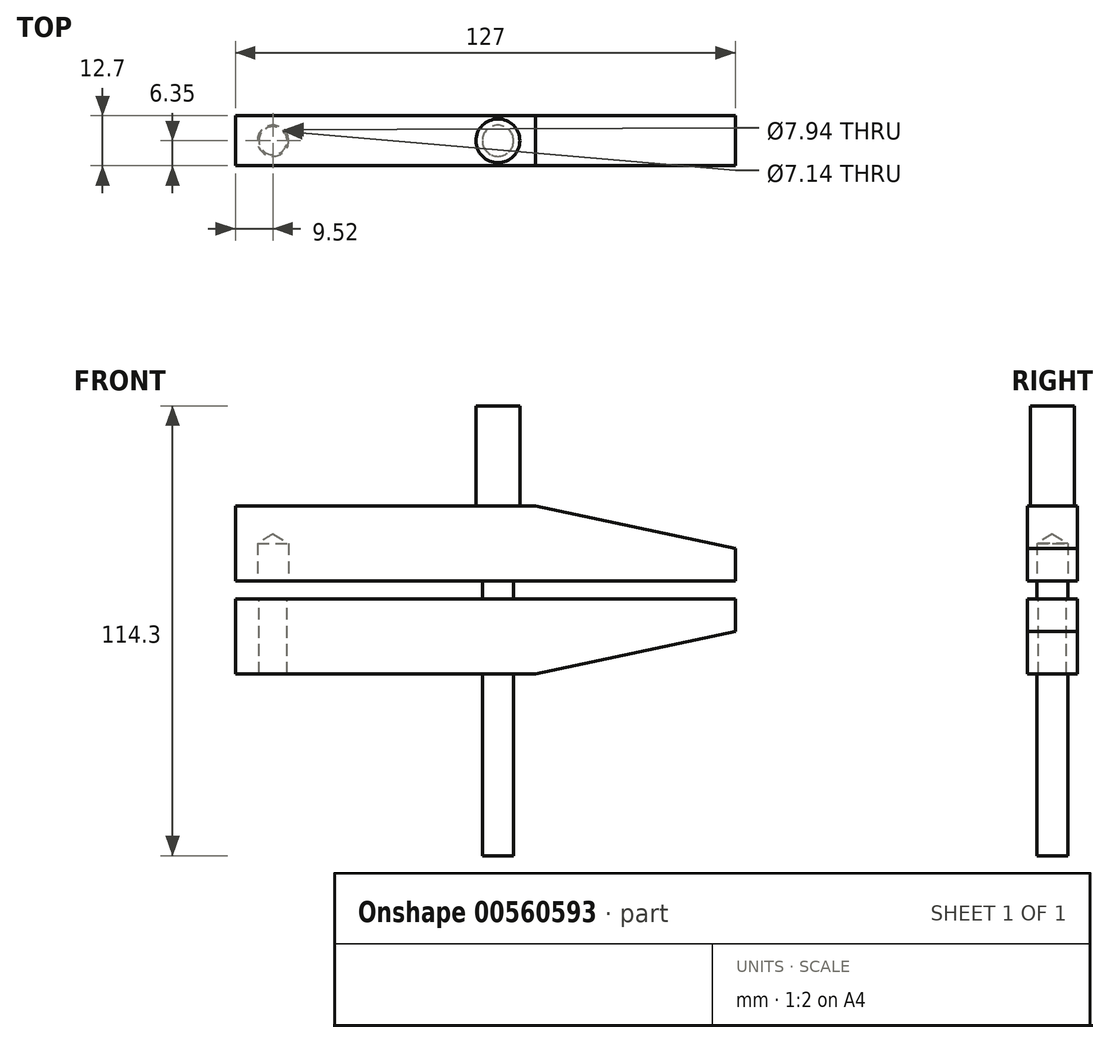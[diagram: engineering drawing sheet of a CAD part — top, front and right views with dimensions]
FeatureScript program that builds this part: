
annotation { "Feature Type Name" : "Feature", "Feature Type Description" : "" }
export const myFeature = defineFeature(function(context is Context, id is Id, definition is map)
    precondition{}
    {
        {
            var Q0;
            Q0=qCreatedBy(makeId("Front.planeOp"),FACE);
            var sketch = newSketch(context, id + "F0", { "sketchPlane" : qUnion([Q0])});
            skLineSegment(sketch, "E0", {"start": v(-59.46, 0) * mm, "end": v(-59.46, 19.05) * mm});
            skLineSegment(sketch, "E1", {"start": v(-59.46, 19.05) * mm, "end": v(16.74, 19.05) * mm});
            skLineSegment(sketch, "E2", {"start": v(16.74, 19.05) * mm, "end": v(67.54, 8.25) * mm});
            skLineSegment(sketch, "E3", {"start": v(67.54, 8.25) * mm, "end": v(67.54, 0) * mm});
            skLineSegment(sketch, "E4", {"start": v(67.54, 0) * mm, "end": v(-59.46, 0) * mm});
            skLineSegment(sketch, "E5", {"start": v(-59.46, -4.6) * mm, "end": v(67.54, -4.6) * mm});
            skLineSegment(sketch, "E6", {"start": v(-59.46, -4.6) * mm, "end": v(-59.46, -23.66) * mm});
            skLineSegment(sketch, "E7", {"start": v(-59.46, -23.66) * mm, "end": v(16.74, -23.66) * mm});
            skLineSegment(sketch, "E8", {"start": v(16.74, -23.66) * mm, "end": v(67.54, -12.86) * mm});
            skLineSegment(sketch, "E9", {"start": v(67.54, -12.86) * mm, "end": v(67.54, -4.6) * mm});
            skSolve(sketch);
        }
        {
            var Q0;
            Q0=makeQuery(id+"F0.imprint","IMPRINT",FACE,{"disambiguationData":[TD([[makeQuery(id+"F0.imprint","IMPRINT",EDGE,{"derivedFrom":sQuery(id+"F0.wireOp",EDGE,"E0")}),-1.0]])]});
            var Q1;
            Q1=makeQuery(id+"F0.imprint","IMPRINT",FACE,{"disambiguationData":[TD([[makeQuery(id+"F0.imprint","IMPRINT",EDGE,{"derivedFrom":sQuery(id+"F0.wireOp",EDGE,"E5")}),-1.0]])]});
            extrude(context, id + "F1", {"entities" : qUnion([Q0, Q1]), "endBound" : BoundingType.SYMMETRIC, "depth" : 12.7 * mm, "offsetDistance" : 25.4 * mm});
        }
        {
            var Q0;
            Q0=makeQuery(id+"F1.opExtrude","SWEPT_FACE",FACE,{"disambiguationData":[OSD([sQuery(id+"F0.wireOp",EDGE,"E4")])]});
            var sketch = newSketch(context, id + "F2", { "sketchPlane" : qUnion([Q0])});
            skCircle(sketch, "E10", {"center": v(7.21, 0) * mm, "radius": 3.97 * mm});
            skCircle(sketch, "E11", {"center": v(-49.94, 0) * mm, "radius": 3.97 * mm});
            skSolve(sketch);
        }
        {
            var Q0;
            Q0=sQuery(id+"F2.wireOp",VERTEX,"E11.center");
            var Q1;
            Q1=makeQuery(id+"F1.opExtrude","SWEPT_BODY",BODY,{"disambiguationData":[OSD([sQuery(id+"F0.wireOp",EDGE,"E0"),sQuery(id+"F0.wireOp",EDGE,"E1"),sQuery(id+"F0.wireOp",EDGE,"E2"),sQuery(id+"F0.wireOp",EDGE,"E3"),sQuery(id+"F0.wireOp",EDGE,"E4")])]});
            hole(context, id + "F3", {"style" : HoleStyle.SIMPLE, "endStyle" : HoleEndStyle.BLIND, "holeDiameter" : 7.94 * mm, "holeDepth" : 9.52 * mm, "isTappedThrough" : true, "tappedDepth" : 12.7 * mm, "tapClearance" : 3, "startFromSketch" : true, "locations" : qUnion([Q0]), "scope" : qUnion([Q1])});
        }
        {
            var Q0;
            Q0=sQuery(id+"F2.wireOp",VERTEX,"E10.center");
            var Q1;
            Q1=makeQuery(id+"F1.opExtrude","SWEPT_BODY",BODY,{"disambiguationData":[OSD([sQuery(id+"F0.wireOp",EDGE,"E0"),sQuery(id+"F0.wireOp",EDGE,"E1"),sQuery(id+"F0.wireOp",EDGE,"E2"),sQuery(id+"F0.wireOp",EDGE,"E3"),sQuery(id+"F0.wireOp",EDGE,"E4")])]});
            hole(context, id + "F4", {"style" : HoleStyle.SIMPLE, "endStyle" : HoleEndStyle.THROUGH, "holeDiameter" : 7.94 * mm, "isTappedThrough" : true, "tappedDepth" : 12.7 * mm, "tapClearance" : 3, "startFromSketch" : true, "locations" : qUnion([Q0]), "scope" : qUnion([Q1])});
        }
        {
            var Q0;
            Q0=sQuery(id+"F2.wireOp",VERTEX,"E11.center");
            var Q1;
            Q1=sQuery(id+"F2.wireOp",VERTEX,"E10.center");
            var Q2;
            Q2=makeQuery(id+"F1.opExtrude","SWEPT_BODY",BODY,{"disambiguationData":[OSD([sQuery(id+"F0.wireOp",EDGE,"E5"),sQuery(id+"F0.wireOp",EDGE,"E6"),sQuery(id+"F0.wireOp",EDGE,"E7"),sQuery(id+"F0.wireOp",EDGE,"E8"),sQuery(id+"F0.wireOp",EDGE,"E9")])]});
            hole(context, id + "F5", {"style" : HoleStyle.SIMPLE, "endStyle" : HoleEndStyle.THROUGH, "oppositeDirection" : true, "holeDiameter" : 7.14 * mm, "isTappedThrough" : true, "tappedDepth" : 12.7 * mm, "tapClearance" : 3, "startFromSketch" : true, "locations" : qUnion([Q0, Q1]), "scope" : qUnion([Q2])});
        }
        {
            var Q0;
            Q0=makeQuery(id+"F1.opExtrude","SWEPT_FACE",FACE,{"disambiguationData":[OSD([sQuery(id+"F0.wireOp",EDGE,"E1")])]});
            var sketch = newSketch(context, id + "F6", { "sketchPlane" : qUnion([Q0])});
            skCircle(sketch, "E12", {"center": v(7.21, 0) * mm, "radius": 3.97 * mm});
            skCircle(sketch, "E13", {"center": v(7.21, 0) * mm, "radius": 5.56 * mm});
            skSolve(sketch);
        }
        {
            var Q0;
            Q0=makeQuery(id+"F6.imprint","IMPRINT",FACE,{"disambiguationData":[TD([[makeQuery(id+"F6.imprint","IMPRINT",EDGE,{"derivedFrom":sQuery(id+"F6.wireOp",EDGE,"E12")}),-1.0]])]});
            var Q1;
            Q1=makeQuery(id+"F6.imprint","IMPRINT",FACE,{"disambiguationData":[TD([[makeQuery(id+"F6.imprint","IMPRINT",EDGE,{"derivedFrom":sQuery(id+"F6.wireOp",EDGE,"E12")}),1.0]])]});
            extrude(context, id + "F7", {"entities" : qUnion([Q0, Q1]), "depth" : 25.4 * mm, "offsetDistance" : 25.4 * mm});
        }
        {
            var Q0;
            Q0=makeQuery(id+"F6.imprint","IMPRINT",FACE,{"disambiguationData":[TD([[makeQuery(id+"F6.imprint","IMPRINT",EDGE,{"derivedFrom":sQuery(id+"F6.wireOp",EDGE,"E12")}),-1.0]])]});
            extrude(context, id + "F8", {"entities" : qUnion([Q0]), "operationType" : NewBodyOperationType.ADD, "oppositeDirection" : true, "depth" : 88.9 * mm, "offsetDistance" : 25.4 * mm});
        }
    });
